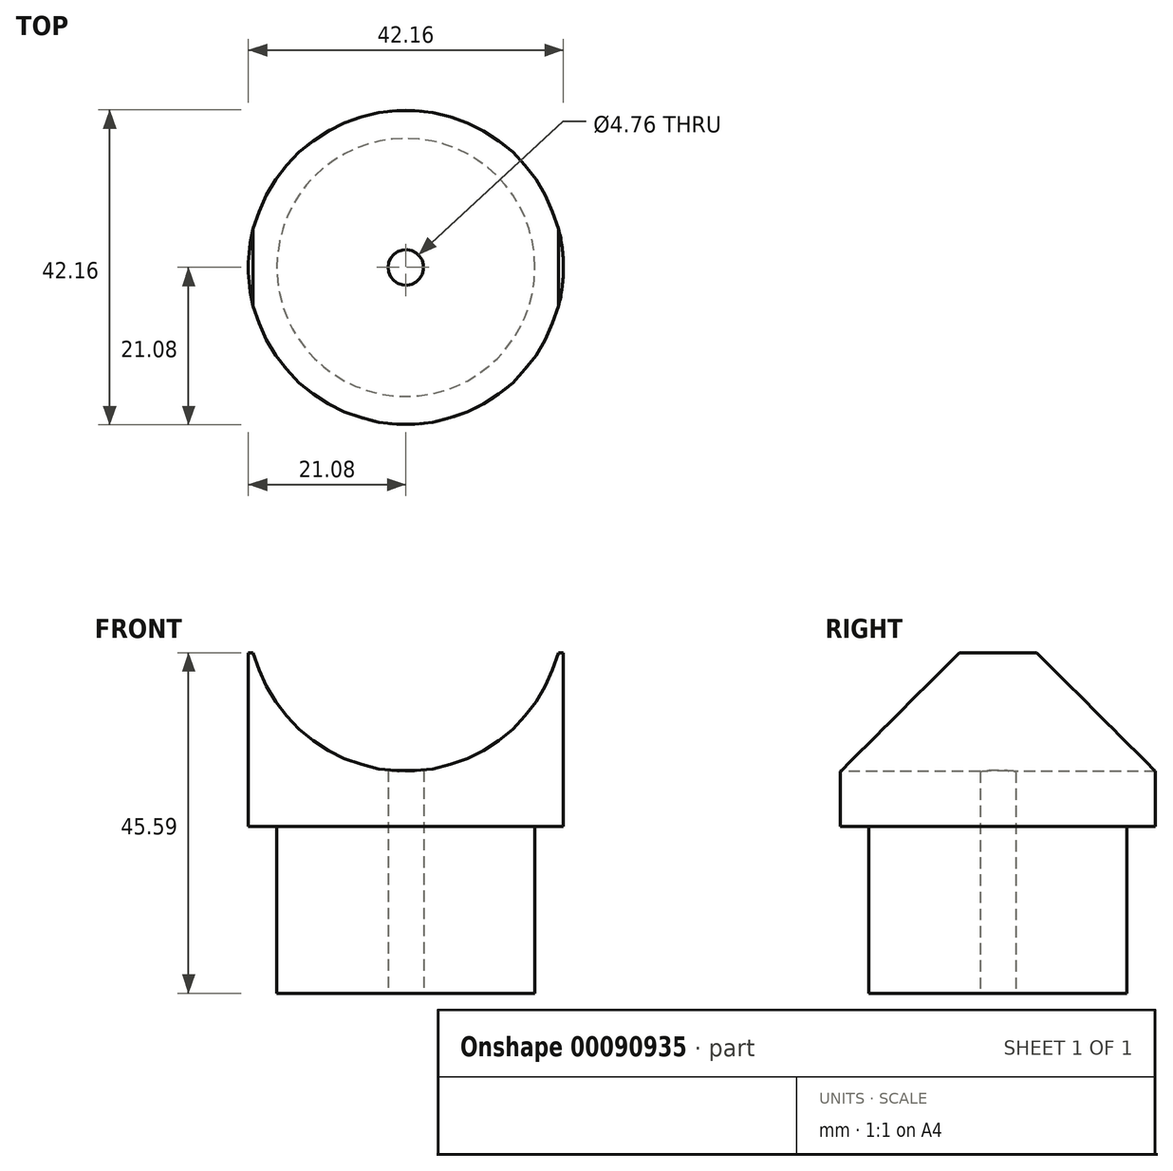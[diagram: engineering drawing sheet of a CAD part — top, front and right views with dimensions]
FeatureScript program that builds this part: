
annotation { "Feature Type Name" : "Feature", "Feature Type Description" : "" }
export const myFeature = defineFeature(function(context is Context, id is Id, definition is map)
    precondition{}
    {
        {
            var Q0;
            Q0=qCreatedBy(makeId("Front.planeOp"),FACE);
            var sketch = newSketch(context, id + "F0", { "sketchPlane" : qUnion([Q0])});
            skLineSegment(sketch, "E0", {"start": v(0, 0) * mm, "end": v(-17.27, 0) * mm});
            skLineSegment(sketch, "E1", {"start": v(-17.27, 0) * mm, "end": v(-17.27, 22.35) * mm});
            skLineSegment(sketch, "E2", {"start": v(-17.27, 22.35) * mm, "end": v(-21.08, 22.35) * mm});
            skLineSegment(sketch, "E3", {"start": v(-21.08, 22.35) * mm, "end": v(-21.08, 45.6) * mm});
            skLineSegment(sketch, "E4", {"start": v(-21.08, 45.6) * mm, "end": v(0, 45.6) * mm});
            skLineSegment(sketch, "E5", {"start": v(0, 45.6) * mm, "end": v(0, 0) * mm});
            skSolve(sketch);
        }
        {
            var Q0;
            Q0 = qSketchRegion(id + "F0", true);
            var Q1;
            Q1=sQuery(id+"F0.wireOp",EDGE,"E5");
            revolve(context, id + "F1", {"entities" : qUnion([Q0]), "axis" : qUnion([Q1]), "revolveType" : RevolveType.FULL});
        }
        {
            var Q0;
            Q0=makeQuery(id+"F1.opRevolve","SWEPT_FACE",FACE,{"disambiguationData":[OSD([sQuery(id+"F0.wireOp",EDGE,"E0")])]});
            var sketch = newSketch(context, id + "F2", { "sketchPlane" : qUnion([Q0])});
            skCircle(sketch, "E6", {"center": v(0, 0) * mm, "radius": 2.38 * mm});
            skSolve(sketch);
        }
        {
            var Q0;
            Q0 = qSketchRegion(id + "F2", true);
            extrude(context, id + "F3", {"entities" : qUnion([Q0]), "operationType" : NewBodyOperationType.REMOVE, "endBound" : BoundingType.THROUGH_ALL, "oppositeDirection" : true, "depth" : 25.4 * mm});
        }
        {
            var Q0;
            Q0=qCreatedBy(makeId("Front.planeOp"),FACE);
            var sketch = newSketch(context, id + "F4", { "sketchPlane" : qUnion([Q0])});
            skCircle(sketch, "E7", {"center": v(0, 50.77) * mm, "radius": 21.08 * mm});
            skSolve(sketch);
        }
        {
            var Q0;
            Q0 = qSketchRegion(id + "F4", true);
            extrude(context, id + "F5", {"entities" : qUnion([Q0]), "operationType" : NewBodyOperationType.REMOVE, "endBound" : BoundingType.THROUGH_ALL, "oppositeDirection" : true, "depth" : 25.4 * mm, "hasSecondDirection" : true, "secondDirectionBound" : SecondDirectionBoundingType.THROUGH_ALL, "secondDirectionOppositeDirection" : false, "secondDirectionDepth" : 25.4 * mm});
        }
    });
